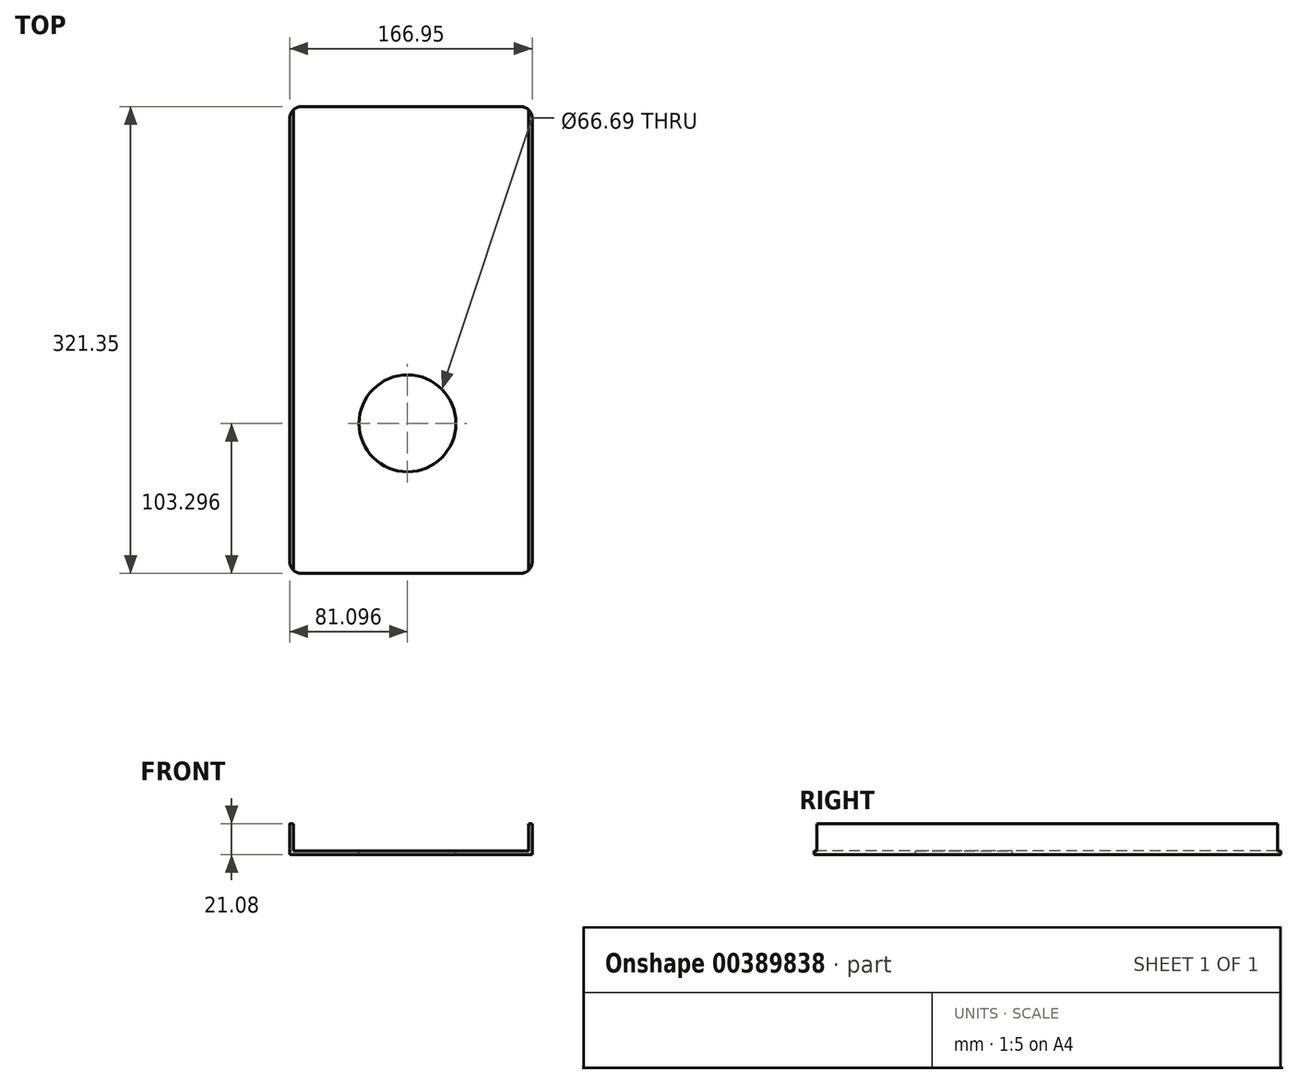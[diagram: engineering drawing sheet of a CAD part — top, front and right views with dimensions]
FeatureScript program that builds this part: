
annotation { "Feature Type Name" : "Feature", "Feature Type Description" : "" }
export const myFeature = defineFeature(function(context is Context, id is Id, definition is map)
    precondition{}
    {
        {
            var Q0;
            Q0=qCreatedBy(makeId("Top.planeOp"),FACE);
            var sketch = newSketch(context, id + "F0", { "sketchPlane" : qUnion([Q0])});
            skLineSegment(sketch, "E0", {"start": v(36.94, 165.53) * mm, "end": v(36.94, -155.82) * mm});
            skLineSegment(sketch, "E1", {"start": v(36.94, -155.82) * mm, "end": v(-130.01, -155.82) * mm});
            skLineSegment(sketch, "E2", {"start": v(-130.01, -155.82) * mm, "end": v(-130.01, 165.53) * mm});
            skLineSegment(sketch, "E3", {"start": v(-130.01, 165.53) * mm, "end": v(36.94, 165.53) * mm});
            skSolve(sketch);
        }
        {
            var Q0;
            Q0=makeQuery(id+"F0.imprint","IMPRINT",FACE,{"disambiguationData":[TD([[makeQuery(id+"F0.imprint","IMPRINT",EDGE,{"derivedFrom":sQuery(id+"F0.wireOp",EDGE,"E0")}),-1.0]])]});
            extrude(context, id + "F1", {"entities" : qUnion([Q0]), "depth" : 21.08 * mm});
        }
        {
            var Q0;
            Q0=makeQuery(id+"F1.opExtrude","CAP_FACE",FACE,{"disambiguationData":[OSD([sQuery(id+"F0.wireOp",EDGE,"E0"),sQuery(id+"F0.wireOp",EDGE,"E1"),sQuery(id+"F0.wireOp",EDGE,"E2"),sQuery(id+"F0.wireOp",EDGE,"E3")])],"isStart":false});
            var Q1;
            Q1=makeQuery(id+"F1.opExtrude","SWEPT_FACE",FACE,{"disambiguationData":[OSD([sQuery(id+"F0.wireOp",EDGE,"E1")])]});
            var Q2;
            Q2=makeQuery(id+"F1.opExtrude","SWEPT_FACE",FACE,{"disambiguationData":[OSD([sQuery(id+"F0.wireOp",EDGE,"E3")])]});
            shell(context, id + "F2", {"entities" : qUnion([Q0, Q1, Q2]), "thickness" : 2.54 * mm});
        }
        {
            var Q0;
            Q0=makeQuery(id+"F1.opExtrude","SWEPT_EDGE",EDGE,{"disambiguationData":[OSD([sQuery(id+"F0.wireOp",EDGE,"E2"),sQuery(id+"F0.wireOp",EDGE,"E3")])]});
            var Q1;
            Q1=makeQuery(id+"F1.opExtrude","SWEPT_EDGE",EDGE,{"disambiguationData":[OSD([sQuery(id+"F0.wireOp",EDGE,"E0"),sQuery(id+"F0.wireOp",EDGE,"E3")])]});
            fillet(context, id + "F3", {"entities" : qUnion([Q0, Q1]), "radius" : 7.97 * mm, "tangentPropagation" : true, "allowEdgeOverflow" : false});
        }
        {
            var Q0;
            Q0=makeQuery(id+"F1.opExtrude","SWEPT_EDGE",EDGE,{"disambiguationData":[OSD([sQuery(id+"F0.wireOp",EDGE,"E0"),sQuery(id+"F0.wireOp",EDGE,"E1")])]});
            var Q1;
            Q1=makeQuery(id+"F1.opExtrude","SWEPT_EDGE",EDGE,{"disambiguationData":[OSD([sQuery(id+"F0.wireOp",EDGE,"E1"),sQuery(id+"F0.wireOp",EDGE,"E2")])]});
            fillet(context, id + "F4", {"entities" : qUnion([Q0, Q1]), "radius" : 7.97 * mm, "tangentPropagation" : true, "allowEdgeOverflow" : false});
        }
        {
            var Q0;
            {var subQ0=sQuery(id+"F0.wireOp",EDGE,"E3");var subQ1=sQuery(id+"F0.wireOp",EDGE,"E2");var subQ2=sQuery(id+"F0.wireOp",EDGE,"E1");var subQ3=sQuery(id+"F0.wireOp",EDGE,"E0");Q0=makeQuery(id+"F2.opShell","OFFSET_FACE",FACE,{"disambiguationData":[OSD([subQ3,subQ2,subQ1,subQ0]),TDD([makeQuery(id+"F1.opExtrude","CAP_FACE",FACE,{"disambiguationData":[OSD([subQ3,subQ2,subQ1,subQ0])],"isStart":true})])]});}
            var sketch = newSketch(context, id + "F5", { "sketchPlane" : qUnion([Q0])});
            skCircle(sketch, "E4", {"center": v(-48.91, -52.52) * mm, "radius": 33.35 * mm});
            skSolve(sketch);
        }
        {
            var Q0;
            Q0=makeQuery(id+"F5.imprint","IMPRINT",FACE,{"disambiguationData":[TD([[makeQuery(id+"F5.imprint","IMPRINT",EDGE,{"derivedFrom":sQuery(id+"F5.wireOp",EDGE,"E4")}),1.0]])]});
            extrude(context, id + "F6", {"entities" : qUnion([Q0]), "operationType" : NewBodyOperationType.REMOVE, "oppositeDirection" : true, "depth" : 145.54 * mm});
        }
    });
